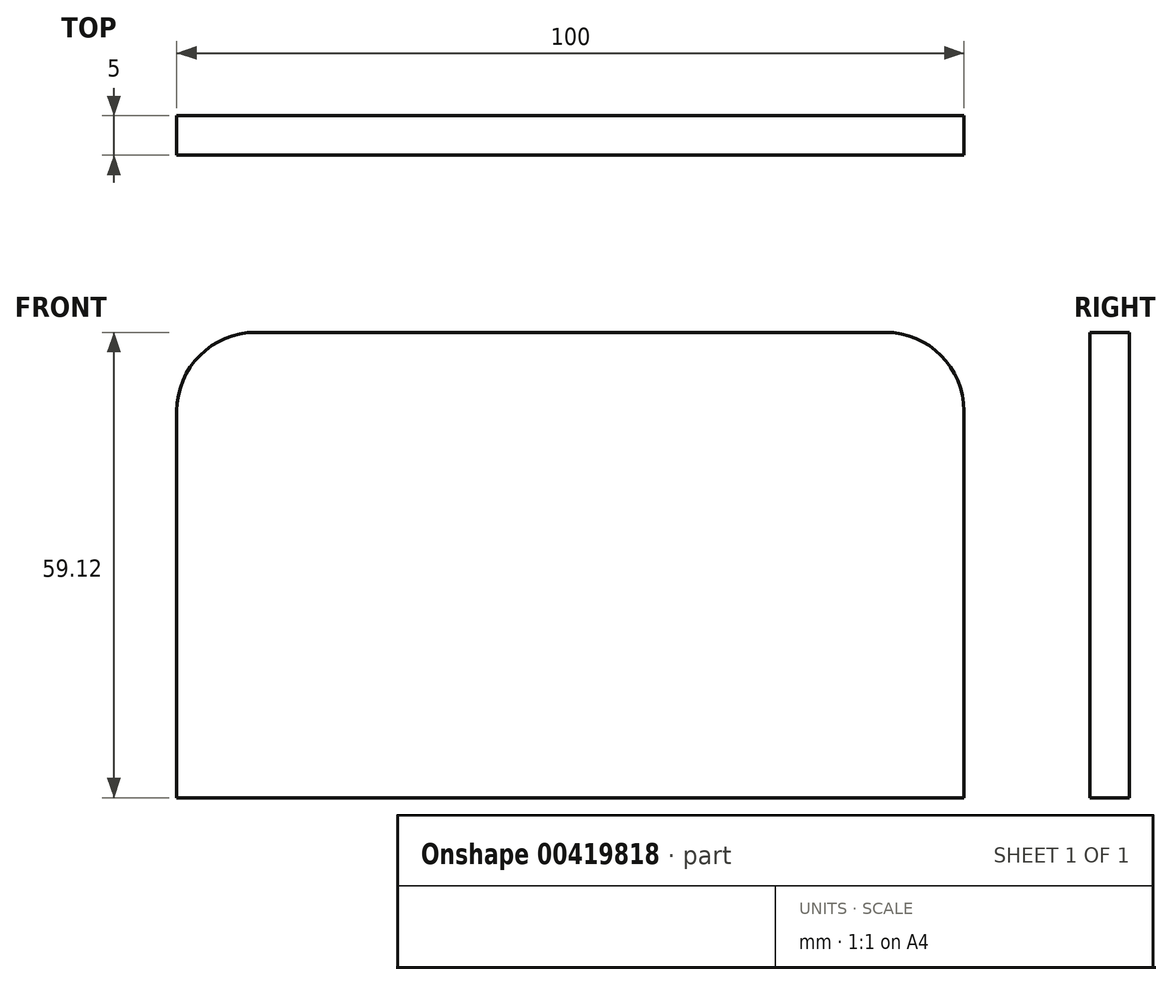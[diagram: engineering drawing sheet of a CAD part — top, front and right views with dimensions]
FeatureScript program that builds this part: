
annotation { "Feature Type Name" : "Feature", "Feature Type Description" : "" }
export const myFeature = defineFeature(function(context is Context, id is Id, definition is map)
    precondition{}
    {
        {
            var Q0;
            Q0=qCreatedBy(makeId("Front.planeOp"),FACE);
            var sketch = newSketch(context, id + "F0", { "sketchPlane" : qUnion([Q0])});
            skLineSegment(sketch, "E0.bottom", {"start": v(0, 0) * mm, "end": v(100, 0) * mm});
            skLineSegment(sketch, "E0.top", {"start": v(0, 59.12) * mm, "end": v(100, 59.12) * mm});
            skLineSegment(sketch, "E0.left", {"start": v(0, 0) * mm, "end": v(0, 59.12) * mm});
            skLineSegment(sketch, "E0.right", {"start": v(100, 0) * mm, "end": v(100, 59.12) * mm});
            skSolve(sketch);
        }
        {
            var Q0;
            Q0 = qSketchRegion(id + "F0", true);
            extrude(context, id + "F1", {"entities" : qUnion([Q0]), "depth" : 5 * mm});
        }
        {
            var Q0;
            Q0=makeQuery(id+"F1.opExtrude","SWEPT_EDGE",EDGE,{"disambiguationData":[OSD([sQuery(id+"F0.wireOp",EDGE,"E0.top"),sQuery(id+"F0.wireOp",EDGE,"E0.right")])]});
            var Q1;
            Q1=makeQuery(id+"F1.opExtrude","SWEPT_EDGE",EDGE,{"disambiguationData":[OSD([sQuery(id+"F0.wireOp",EDGE,"E0.top"),sQuery(id+"F0.wireOp",EDGE,"E0.left")])]});
            fillet(context, id + "F2", {"entities" : qUnion([Q0, Q1]), "radius" : 10 * mm, "tangentPropagation" : true, "allowEdgeOverflow" : false});
        }
    });
